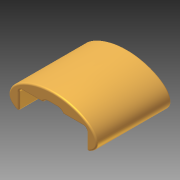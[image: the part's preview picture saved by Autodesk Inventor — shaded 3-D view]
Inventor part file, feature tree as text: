
AUTODESK INVENTOR PART (.ipt)
format: ipt  version: 2011 (Build 150239000, 239)  size: 240,128 bytes
history: native  units: mm (DEFAULTED — no unit token found)
features: fillet x5, extrude x3, sketch x3, plane x1, mirror x1
ambient origin geometry x8: Origin, YZ Plane, XZ Plane, XY Plane, X Axis, Y Axis, Z Axis, Center Point
bodies: Solid1 (feature_tree)
feature tree (13):
  extrude  "Extrusion1"  Depth=17.4752mm TaperAngle=0.0deg
  fillet  "Fillet1"  Radius=15.875mm
  extrude  "Extrusion2"  Depth=12.217305mm
  fillet  "Fillet2"  Radius=12.217305mm
  fillet  "Fillet3"  Radius=0.762mm
  fillet  "Fillet5"  Radius=3.9624mm
  fillet  "Fillet4"  Radius=4.7752mm
  plane  "Work Plane1"
  extrude  "Extrusion3"  Depth=1.524mm
  mirror  "Mirror1"
  sketch  "Sketch1"  dims[d1=4.7752mm d2=17.4752mm d3=0.0mm d4=15.875mm]
  sketch  "Sketch2"  dims[d5=20.6248mm d6=12.217305mm d7=12.217305mm d8=0.762mm d9=3.9624mm d10=4.7752mm]
  sketch  "Sketch3"  dims[d11=0.762mm d12=0.0mm d13=1.524mm d14=0.381mm d15=0.381mm d16=0.381mm d17=0.381mm d18=6.35mm d19=1.524mm d20=0.762mm d21=0.381mm d22=3.175mm d23=0.0mm]
